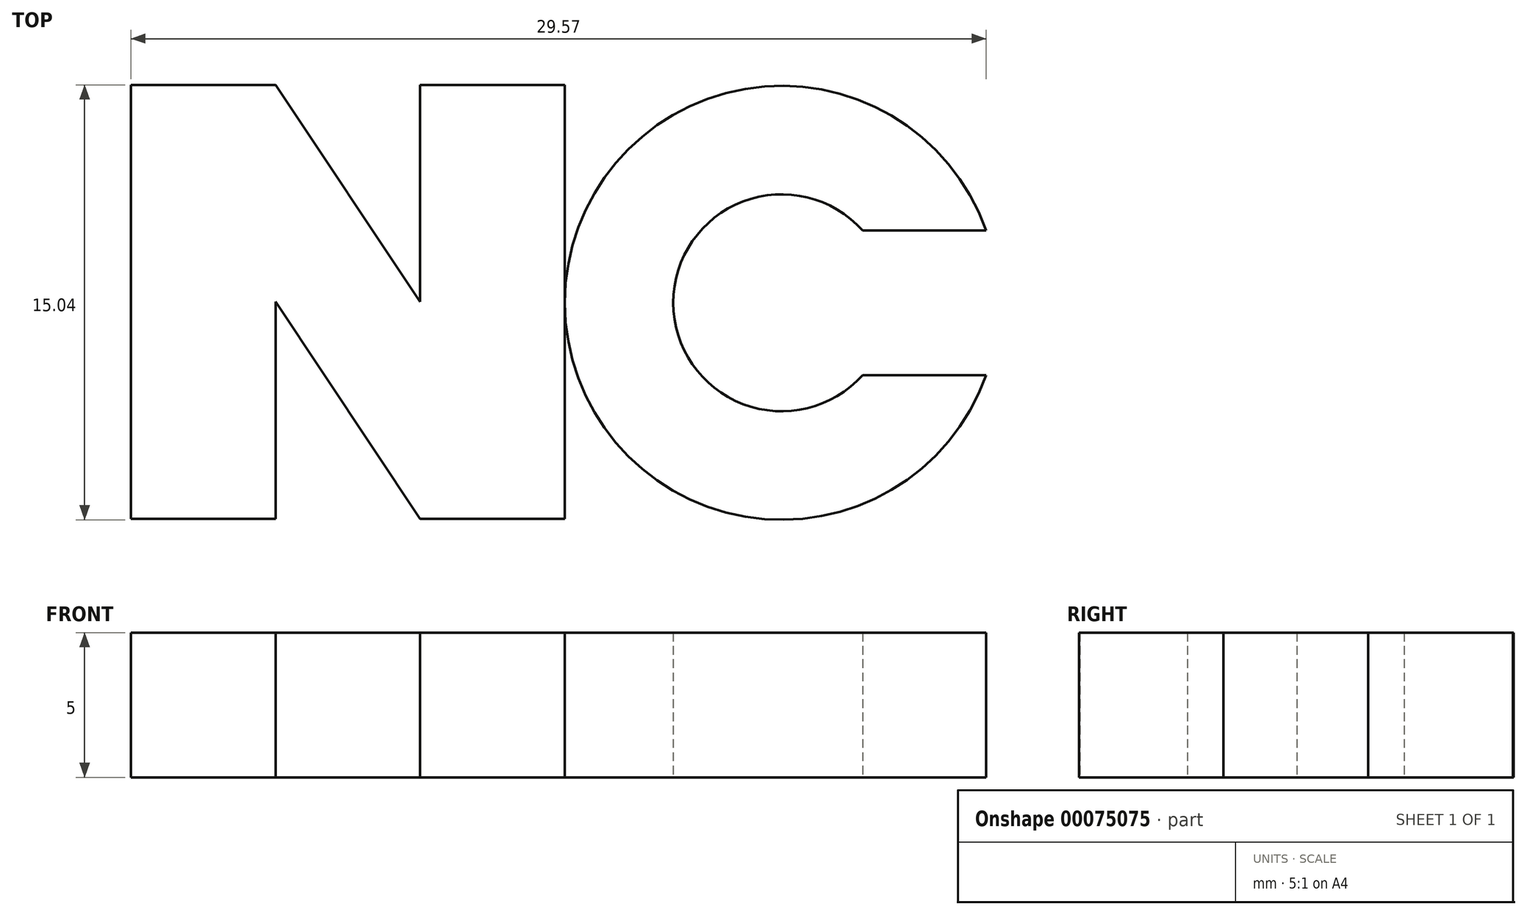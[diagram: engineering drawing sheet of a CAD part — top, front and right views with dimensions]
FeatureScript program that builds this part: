
annotation { "Feature Type Name" : "Feature", "Feature Type Description" : "" }
export const myFeature = defineFeature(function(context is Context, id is Id, definition is map)
    precondition{}
    {
        {
            var Q0;
            Q0=qCreatedBy(makeId("Top.planeOp"),FACE);
            var sketch = newSketch(context, id + "F0", { "sketchPlane" : qUnion([Q0])});
            skLineSegment(sketch, "E0", {"start": v(-15, -15) * mm, "end": v(-10, -15) * mm});
            skLineSegment(sketch, "E1", {"start": v(-10, -15) * mm, "end": v(-10, -7.5) * mm});
            skLineSegment(sketch, "E2", {"start": v(-10, -7.5) * mm, "end": v(-5, -15) * mm});
            skLineSegment(sketch, "E3", {"start": v(-5, -15) * mm, "end": v(0, -15) * mm});
            skLineSegment(sketch, "E4", {"start": v(0, -15) * mm, "end": v(0, 0) * mm});
            skLineSegment(sketch, "E5", {"start": v(0, 0) * mm, "end": v(-5, 0) * mm});
            skLineSegment(sketch, "E6", {"start": v(-5, 0) * mm, "end": v(-5, -7.5) * mm});
            skLineSegment(sketch, "E7", {"start": v(-5, -7.5) * mm, "end": v(-10, 0) * mm});
            skLineSegment(sketch, "E8", {"start": v(-10, 0) * mm, "end": v(-15, 0) * mm});
            skLineSegment(sketch, "E9", {"start": v(-15, 0) * mm, "end": v(-15, -15) * mm});
            skSolve(sketch);
        }
        {
            var Q0;
            Q0=makeQuery(id+"F0.imprint","IMPRINT",FACE,{"disambiguationData":[TD([[makeQuery(id+"F0.imprint","IMPRINT",EDGE,{"derivedFrom":sQuery(id+"F0.wireOp",EDGE,"E0")}),1.0]])]});
            extrude(context, id + "F1", {"entities" : qUnion([Q0]), "depth" : 5 * mm});
        }
        {
            var Q0;
            Q0=qCreatedBy(makeId("Top.planeOp"),FACE);
            var sketch = newSketch(context, id + "F2", { "sketchPlane" : qUnion([Q0])});
            skCircle(sketch, "E10", {"center": v(7.5, -7.54) * mm, "radius": 7.5 * mm});
            skCircle(sketch, "E11", {"center": v(7.5, -7.54) * mm, "radius": 3.75 * mm});
            skLineSegment(sketch, "E12", {"start": v(7.5, -7.54) * mm, "end": v(15, -7.54) * mm, "construction": true});
            skLineSegment(sketch, "E13", {"start": v(10.3, -5.04) * mm, "end": v(14.57, -5.04) * mm});
            skLineSegment(sketch, "E14", {"start": v(10.3, -10.04) * mm, "end": v(14.57, -10.04) * mm});
            skSolve(sketch);
        }
        {
            var Q0;
            {var subQ0=sQuery(id+"F2.wireOp",EDGE,"E13");Q0=makeQuery(id+"F2.imprint","IMPRINT",FACE,{"disambiguationData":[TD([[makeQuery(id+"F2.imprint","IMPRINT",EDGE,{"derivedFrom":subQ0}),1.0]])]});}
            extrude(context, id + "F3", {"entities" : qUnion([Q0]), "operationType" : NewBodyOperationType.ADD, "depth" : 5 * mm});
        }
    });
